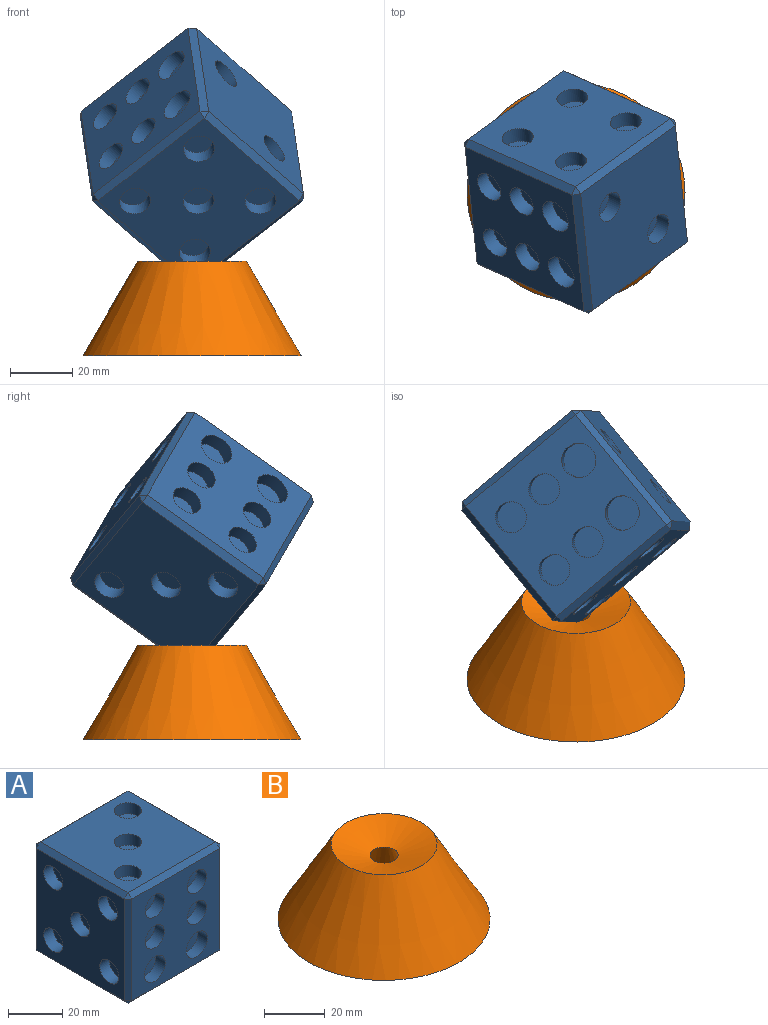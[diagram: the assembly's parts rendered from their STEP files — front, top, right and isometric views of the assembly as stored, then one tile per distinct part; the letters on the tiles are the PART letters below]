
ASSEMBLY  parts=2 mates=1
PART A: 68 faces, bbox 50x50x50 mm
  f0: plane 46x46mm, normal (0,0,-1), area 1958.9mm2, adj f44,f46,f54,f55,f63,f64
  f1: plane 46x46mm, normal (1,0,0), area 1801.8mm2, adj f36,f38,f40,f42,f48,f51,f55,f56
  f2: plane 46x46mm, normal (-1,0,0), area 1723.3mm2, adj f26,f28,f30,f32,f34,f53,f62,f63
  f3: plane 46x46mm, normal (0,-1,0), area 1609.4mm2, adj f8,f10,f12,f14,f16,f18,f48,f52
  f4: plane 46x46mm, normal (0,1,0), area 2037.5mm2, adj f6,f56,f61,f64,f67
  f5: plane 46x46mm, normal (0,0,1), area 1880.4mm2, adj f20,f22,f24,f51,f52,f61,f62
  f6: cylinder r=5mm len=10mm, axis (0,1,0), area 157.1mm2, adj f4,f7
  f7: plane 10x10mm, normal (0,1,0), area 78.5mm2, adj f6
  f8: cylinder r=5mm len=10mm, axis (0,-1,0), area 157.1mm2, adj f3,f9
  f9: plane 10x10mm, normal (0,-1,0), area 78.5mm2, adj f8
  f10: cylinder r=5.53mm len=11.07mm, axis (0,-1,0), area 173.9mm2, adj f3,f11
  f11: plane 11.07x11.07mm, normal (0,-1,0), area 96.2mm2, adj f10
  f12: cylinder r=5mm len=10mm, axis (0,-1,0), area 157.1mm2, adj f3,f13
  f13: plane 10x10mm, normal (0,-1,0), area 78.5mm2, adj f12
  f14: cylinder r=5mm len=10mm, axis (0,-1,0), area 157.1mm2, adj f3,f15
  f15: plane 10x10mm, normal (0,-1,0), area 78.5mm2, adj f14
  f16: cylinder r=5mm len=10mm, axis (0,-1,0), area 157.1mm2, adj f3,f17
  f17: plane 10x10mm, normal (0,-1,0), area 78.5mm2, adj f16
  f18: cylinder r=5.53mm len=11.07mm, axis (0,-1,0), area 173.9mm2, adj f3,f19
  f19: plane 11.07x11.07mm, normal (0,-1,0), area 96.2mm2, adj f18
  f20: cylinder r=5mm len=10mm, axis (0,0,1), area 157.1mm2, adj f5,f21
  f21: plane 10x10mm, normal (0,0,1), area 78.5mm2, adj f20
  f22: cylinder r=5mm len=10mm, axis (0,0,1), area 157.1mm2, adj f5,f23
  f23: plane 10x10mm, normal (0,0,1), area 78.5mm2, adj f22
  f24: cylinder r=5mm len=10mm, axis (0,0,1), area 157.1mm2, adj f5,f25
  f25: plane 10x10mm, normal (0,0,1), area 78.5mm2, adj f24
  f26: cylinder r=5mm len=10mm, axis (-1,0,0), area 157.1mm2, adj f2,f27
  f27: plane 10x10mm, normal (-1,0,0), area 78.5mm2, adj f26
  f28: cylinder r=5mm len=10mm, axis (-1,0,0), area 157.1mm2, adj f2,f29
  f29: plane 10x10mm, normal (-1,0,0), area 78.5mm2, adj f28
  f30: cylinder r=5mm len=10mm, axis (-1,0,0), area 157.1mm2, adj f2,f31
  f31: plane 10x10mm, normal (-1,0,0), area 78.5mm2, adj f30
  f32: cylinder r=5mm len=10mm, axis (-1,0,0), area 157.1mm2, adj f2,f33
  f33: plane 10x10mm, normal (-1,0,0), area 78.5mm2, adj f32
  f34: cylinder r=5mm len=10mm, axis (-1,0,0), area 157.1mm2, adj f2,f35
  f35: plane 10x10mm, normal (-1,0,0), area 78.5mm2, adj f34
  f36: cylinder r=5mm len=10mm, axis (1,0,0), area 157.1mm2, adj f1,f37
  f37: plane 10x10mm, normal (1,0,0), area 78.5mm2, adj f36
  f38: cylinder r=5mm len=10mm, axis (1,0,0), area 157.1mm2, adj f1,f39
  f39: plane 10x10mm, normal (1,0,0), area 78.5mm2, adj f38
  f40: cylinder r=5mm len=10mm, axis (1,0,0), area 157.1mm2, adj f1,f41
  f41: plane 10x10mm, normal (1,0,0), area 78.5mm2, adj f40
  f42: cylinder r=5mm len=10mm, axis (1,0,0), area 157.1mm2, adj f1,f43
  f43: plane 10x10mm, normal (1,0,0), area 78.5mm2, adj f42
  f44: cylinder r=5mm len=10mm, axis (0,0,-1), area 157.1mm2, adj f0,f45
  f45: plane 10x10mm, normal (0,0,-1), area 78.5mm2, adj f44
  f46: cylinder r=5mm len=10mm, axis (0,0,-1), area 157.1mm2, adj f0,f47
  f47: plane 10x10mm, normal (0,0,-1), area 78.5mm2, adj f46
  f48: plane 46x2mm, normal (0.71,-0.71,0), area 130.1mm2, adj f1,f3,f49,f50
  f49: plane 2x2mm, normal (0.58,-0.58,0.58), area 3.5mm2, adj f48,f51,f52
  f50: plane 2x2mm, normal (0.58,-0.58,-0.58), area 3.5mm2, adj f48,f54,f55
  f51: plane 46x2mm, normal (0.71,0,0.71), area 130.1mm2, adj f1,f5,f49,f57
  f52: plane 46x2mm, normal (0,-0.71,0.71), area 130.1mm2, adj f3,f5,f49,f58
  f53: plane 46x2mm, normal (-0.71,-0.71,0), area 130.1mm2, adj f2,f3,f58,f59
  f54: plane 46x2mm, normal (0,-0.71,-0.71), area 130.1mm2, adj f0,f3,f50,f59
  f55: plane 46x2mm, normal (0.71,0,-0.71), area 130.1mm2, adj f0,f1,f50,f60
  f56: plane 46x2mm, normal (0.71,0.71,0), area 130.1mm2, adj f1,f4,f57,f60
  f57: plane 2x2mm, normal (0.58,0.58,0.58), area 3.5mm2, adj f51,f56,f61
  f58: plane 2x2mm, normal (-0.58,-0.58,0.58), area 3.5mm2, adj f52,f53,f62
  f59: plane 2x2mm, normal (-0.58,-0.58,-0.58), area 3.5mm2, adj f53,f54,f63
  f60: plane 2x2mm, normal (0.58,0.58,-0.58), area 3.5mm2, adj f55,f56,f64
  f61: plane 46x2mm, normal (0,0.71,0.71), area 130.1mm2, adj f4,f5,f57,f65
  f62: plane 46x2mm, normal (-0.71,0,0.71), area 130.1mm2, adj f2,f5,f58,f65
  f63: plane 46x2mm, normal (-0.71,0,-0.71), area 130.1mm2, adj f0,f2,f59,f66
  f64: plane 46x2mm, normal (0,0.71,-0.71), area 130.1mm2, adj f0,f4,f60,f66
  f65: plane 2x2mm, normal (-0.58,0.58,0.58), area 3.5mm2, adj f61,f62,f67
  f66: plane 2x2mm, normal (-0.58,0.58,-0.58), area 3.5mm2, adj f63,f64,f67
  f67: plane 46x2mm, normal (-0.71,0.71,0), area 130.1mm2, adj f2,f4,f65,f66
PART B: 4 faces, bbox 70x70x30.3 mm
  f0: cone r=17.5mm half-angle=70.9deg, axis (0,0,1), area 945.6mm2, adj f1,f3
  f1: cone r=17.5mm half-angle=30deg, axis (0,0,-1), area 5772.7mm2, adj f0,f2
  f2: plane 70x70mm, normal (0,0,-1), area 3265.6mm2, adj f1,f3
  f3: cone r=4.67mm half-angle=19.1deg, axis (0,0,-1), area 1573.1mm2, adj f0,f2
PLACE A rot(axis=(-0.56,-0.82,0.09),126.2deg) t=(34.09,-30.4,34.34)mm
PLACE B t=(34.09,-30.4,-29.76)mm fixed
MATE cylindrical A.f65 <-> B.f3  axis (0,0,-1) through (34.09,-30.4,-6.65)mm
